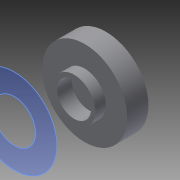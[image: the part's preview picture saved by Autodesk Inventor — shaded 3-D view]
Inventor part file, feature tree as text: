
AUTODESK INVENTOR PART (.ipt)
format: ipt  version: 2015 SP1 (Build 190203100, 203)  size: 121,344 bytes
history: native  units: in
note: dims shown in document units (in); Inventor stores cm internally (conversion verified against a paired STEP export)
features: extrude x4, sketch x4, projected_geometry x2, shell x1, reference x1
ambient origin geometry x8: Origin, YZ Plane, XZ Plane, XY Plane, X Axis, Y Axis, Z Axis, Center Point
bodies: Solid1 (feature_tree)
feature tree (12):
  extrude  "Extrusion1"  Depth=0.5in TaperAngle=0.0deg
  extrude  "Extrusion2"  Depth=0.25in TaperAngle=0.0deg
  shell  "Shell1"  Thickness=0.1in
  extrude  "Extrusion3"  Depth=0.25in
  extrude  "Extrusion4"  Depth=0.0098in
  sketch  "Sketch1"  dims[d0=2.0in d1=0.5in d2=0.0in]
  reference  "Reference1"
  sketch  "Sketch2"  dims[d3=1.0in d4=0.25in d5=0.0in d6=0.1in]
  projected_geometry  "Projected Loop1"
  sketch  "Sketch3"  dims[d7=0.35in d8=0.25in]
  sketch  "Sketch4"  dims[d9=0.0394in d10=0.0in d11=0.0098in d12=0.0394in d13=0.0in]
  projected_geometry  "Projected Loop2"
